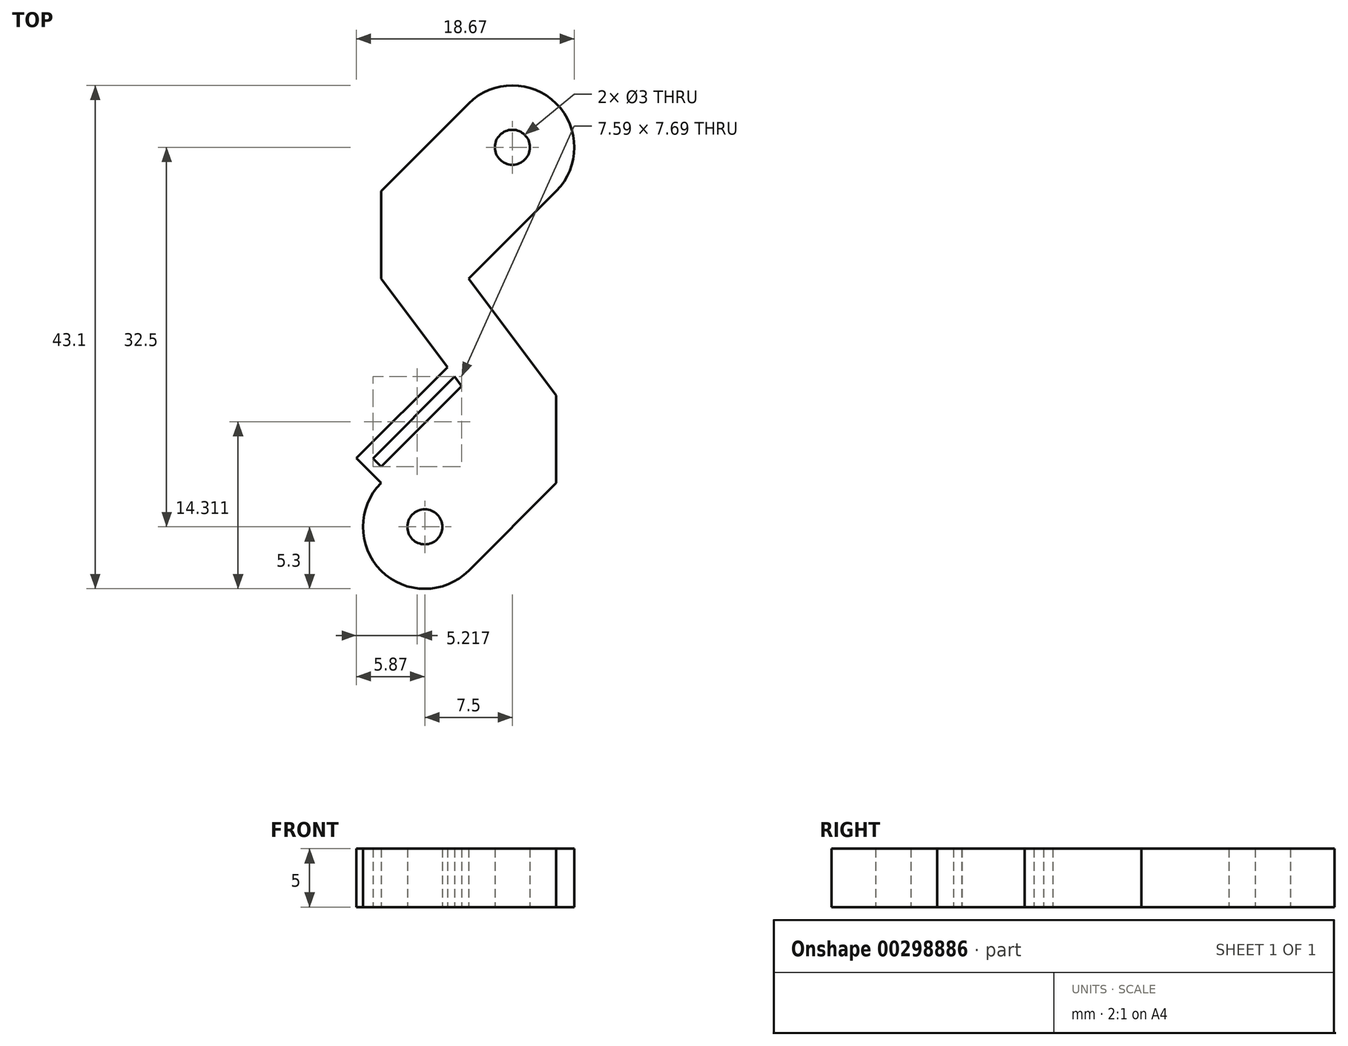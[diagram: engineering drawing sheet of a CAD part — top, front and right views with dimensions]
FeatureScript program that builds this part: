
annotation { "Feature Type Name" : "Feature", "Feature Type Description" : "" }
export const myFeature = defineFeature(function(context is Context, id is Id, definition is map)
    precondition{}
    {
        {
            var Q0;
            Q0=qCreatedBy(makeId("Top.planeOp"),FACE);
            var sketch = newSketch(context, id + "F0", { "sketchPlane" : qUnion([Q0])});
            skLineSegment(sketch, "E0.left", {"start": v(7.5, -12.5) * mm, "end": v(7.5, -5) * mm});
            skLineSegment(sketch, "E0.right", {"start": v(-7.5, 5) * mm, "end": v(-7.5, 12.5) * mm});
            skPoint(sketch, "E0.middle", {"position": v(0, 0) * mm});
            skLineSegment(sketch, "E1.left", {"start": v(-7.5, 12.5) * mm, "end": v(-7.5, 5) * mm});
            skLineSegment(sketch, "E2", {"start": v(-7.5, -12.5) * mm, "end": v(0, -5) * mm});
            skLineSegment(sketch, "E3", {"start": v(0, -20) * mm, "end": v(7.5, -12.5) * mm});
            skLineSegment(sketch, "E4", {"start": v(0, 5) * mm, "end": v(7.5, 12.5) * mm});
            skLineSegment(sketch, "E5", {"start": v(0, 20) * mm, "end": v(-7.5, 12.5) * mm});
            skLineSegment(sketch, "E6", {"start": v(0, 5) * mm, "end": v(7.5, -5) * mm});
            skLineSegment(sketch, "E7", {"start": v(-7.5, 5) * mm, "end": v(0, -5) * mm});
            skArc(sketch, "E8", {"start": v(7.5, 12.5) * mm, "mid": v(7.5, 20) * mm, "end": v(0, 20) * mm});
            skArc(sketch, "E9", {"start": v(-7.5, -12.5) * mm, "mid": v(-7.5, -20) * mm, "end": v(0, -20) * mm});
            skPoint(sketch, "E10.orphan", {"position": v(7.5, 20) * mm});
            skPoint(sketch, "E11.orphan", {"position": v(-7.5, -20) * mm});
            skCircle(sketch, "E12", {"center": v(3.75, 16.25) * mm, "radius": 1.5 * mm});
            skCircle(sketch, "E13", {"center": v(-3.75, -16.25) * mm, "radius": 1.5 * mm});
            skSolve(sketch);
        }
        {
            var Q0;
            Q0 = qSketchRegion(id + "F0", true);
            extrude(context, id + "F1", {"entities" : qUnion([Q0]), "depth" : 5 * mm});
        }
        {
            var Q0;
            Q0=makeQuery(id+"F1.opExtrude","CAP_FACE",FACE,{"disambiguationData":[OSD([sQuery(id+"F0.wireOp",EDGE,"E1.left"),sQuery(id+"F0.wireOp",EDGE,"E0.left"),sQuery(id+"F0.wireOp",EDGE,"E2"),sQuery(id+"F0.wireOp",EDGE,"E3"),sQuery(id+"F0.wireOp",EDGE,"E4"),sQuery(id+"F0.wireOp",EDGE,"E5"),sQuery(id+"F0.wireOp",EDGE,"E6"),sQuery(id+"F0.wireOp",EDGE,"E7"),sQuery(id+"F0.wireOp",EDGE,"E8"),sQuery(id+"F0.wireOp",EDGE,"E9"),sQuery(id+"F0.wireOp",EDGE,"E12"),sQuery(id+"F0.wireOp",EDGE,"E13")])],"isStart":true});
            var sketch = newSketch(context, id + "F2", { "sketchPlane" : qUnion([Q0])});
            skLineSegment(sketch, "E14", {"start": v(0, 5) * mm, "end": v(-7.5, 12.5) * mm});
            skLineSegment(sketch, "E15", {"start": v(-7.5, 12.5) * mm, "end": v(-9.62, 10.38) * mm});
            skLineSegment(sketch, "E16", {"start": v(-9.62, 10.38) * mm, "end": v(-1.82, 2.58) * mm});
            skLineSegment(sketch, "E17", {"start": v(-7.5, 12.5) * mm, "end": v(-8.2, 11.8) * mm});
            skLineSegment(sketch, "E18", {"start": v(-8.2, 11.8) * mm, "end": v(-0.6, 4.2) * mm});
            skLineSegment(sketch, "E19", {"start": v(-0.6, 4.2) * mm, "end": v(-1.2, 3.4) * mm});
            skLineSegment(sketch, "E20", {"start": v(-1.2, 3.4) * mm, "end": v(-8.9, 11.1) * mm});
            skLineSegment(sketch, "E21", {"start": v(-1.82, 2.58) * mm, "end": v(-1.2, 3.4) * mm});
            skLineSegment(sketch, "E22", {"start": v(-0.6, 4.2) * mm, "end": v(0, 5) * mm});
            skLineSegment(sketch, "E23", {"start": v(-9.62, 10.38) * mm, "end": v(-8.91, 9.67) * mm});
            skLineSegment(sketch, "E24", {"start": v(-8.91, 9.67) * mm, "end": v(-6.8, 11.8) * mm});
            skSolve(sketch);
        }
        {
            var Q0;
            Q0=makeQuery(id+"F2.imprint","IMPRINT",FACE,{"disambiguationData":[TD([[makeQuery(id+"F2.imprint","IMPRINT",EDGE,{"derivedFrom":sQuery(id+"F2.wireOp",EDGE,"E14")}),-1.0]])]});
            var Q1;
            {var subQ0=sQuery(id+"F2.wireOp",EDGE,"E16");Q1=makeQuery(id+"F2.imprint","IMPRINT",FACE,{"disambiguationData":[TD([[makeQuery(id+"F2.imprint","IMPRINT",EDGE,{"derivedFrom":subQ0}),1.0]])]});}
            var Q2;
            {var subQ0=sQuery(id+"F2.wireOp",EDGE,"E23");Q2=makeQuery(id+"F2.imprint","IMPRINT",FACE,{"disambiguationData":[TD([[makeQuery(id+"F2.imprint","IMPRINT",EDGE,{"derivedFrom":subQ0}),1.0]])]});}
            var Q3;
            {var subQ1=sQuery(id+"F2.wireOp",EDGE,"E15");var subQ3=sQuery(id+"F2.wireOp",EDGE,"E20");var subQ4=makeQuery(id+"F2.imprint","INTERSECT",VERTEX,{"derivedFrom":[subQ1,subQ3]});Q3=makeQuery(id+"F2.imprint","IMPRINT",FACE,{"disambiguationData":[TD([[makeQuery(id+"F2.imprint","IMPRINT",EDGE,{"disambiguationData":[TD([[subQ4,1.0]])],"derivedFrom":subQ3}),-1.0]])]});}
            extrude(context, id + "F3", {"entities" : qUnion([Q0, Q1, Q2, Q3]), "operationType" : NewBodyOperationType.ADD, "oppositeDirection" : true, "depth" : 5 * mm});
        }
    });
